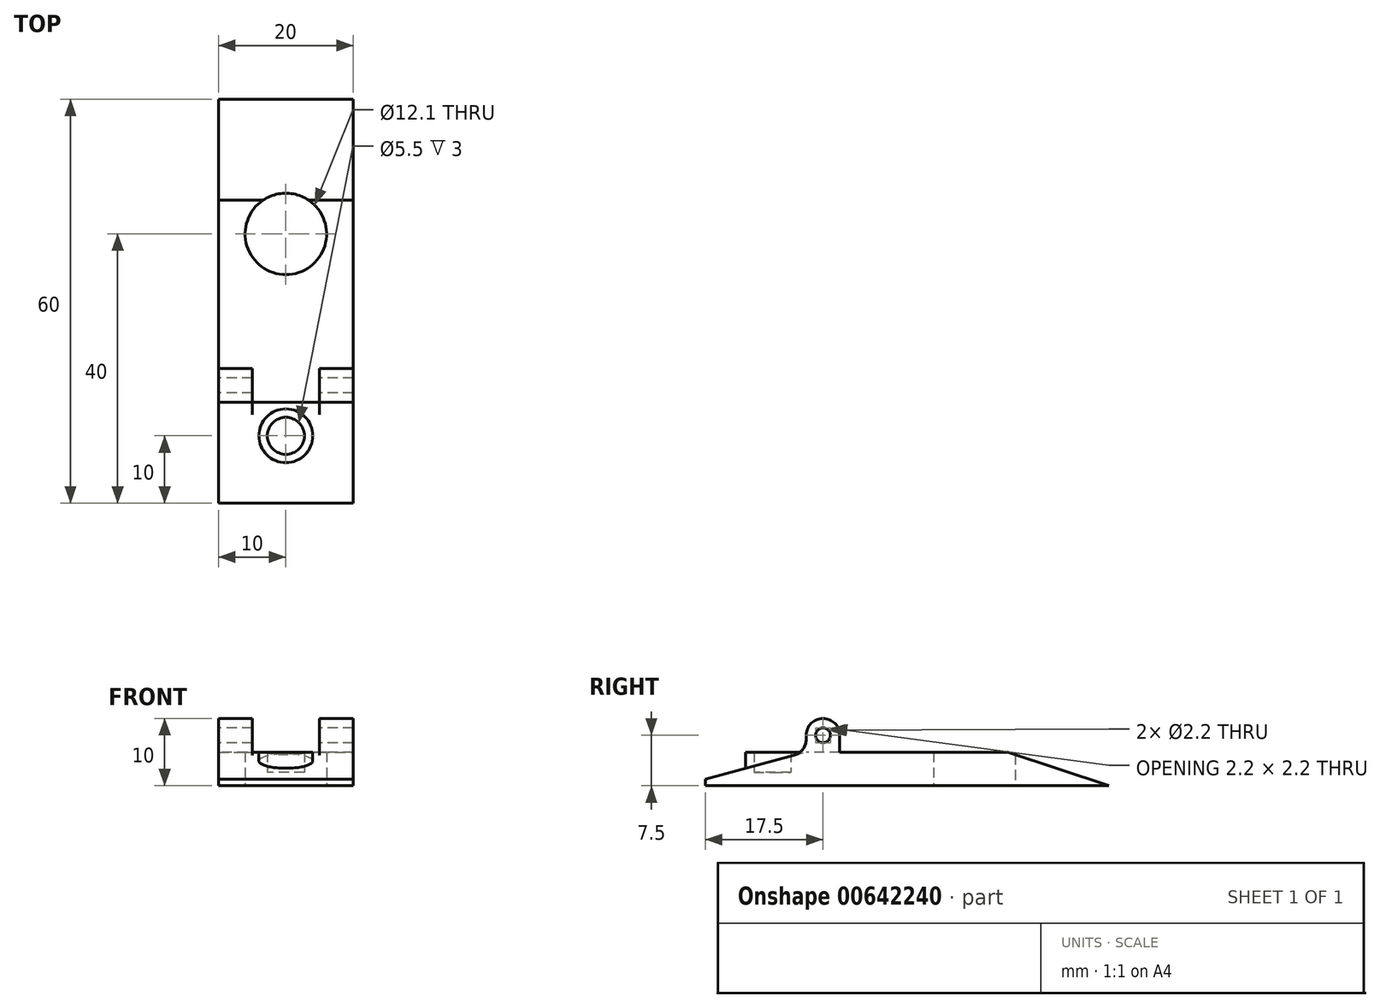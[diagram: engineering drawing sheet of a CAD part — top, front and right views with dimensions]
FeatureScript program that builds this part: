
annotation { "Feature Type Name" : "Feature", "Feature Type Description" : "" }
export const myFeature = defineFeature(function(context is Context, id is Id, definition is map)
    precondition{}
    {
        {
            var Q0;
            Q0=qCreatedBy(makeId("Top.planeOp"),FACE);
            var sketch = newSketch(context, id + "F0", { "sketchPlane" : qUnion([Q0])});
            skLineSegment(sketch, "E0.bottom", {"start": v(0, 0) * mm, "end": v(20, 0) * mm});
            skLineSegment(sketch, "E0.top", {"start": v(0, 60) * mm, "end": v(20, 60) * mm});
            skLineSegment(sketch, "E0.left", {"start": v(0, 0) * mm, "end": v(0, 60) * mm});
            skLineSegment(sketch, "E0.right", {"start": v(20, 0) * mm, "end": v(20, 60) * mm});
            skCircle(sketch, "E1", {"center": v(10, 40) * mm, "radius": 6.05 * mm});
            skCircle(sketch, "E2", {"center": v(10, 10) * mm, "radius": 2.75 * mm});
            skCircle(sketch, "E3", {"center": v(10, 40) * mm, "radius": 2 * mm});
            skCircle(sketch, "E4", {"center": v(10, 10) * mm, "radius": 4 * mm});
            skSolve(sketch);
        }
        {
            var Q0;
            Q0=makeQuery(id+"F0.imprint","IMPRINT",FACE,{"disambiguationData":[TD([[makeQuery(id+"F0.imprint","IMPRINT",EDGE,{"derivedFrom":sQuery(id+"F0.wireOp",EDGE,"E0.bottom")}),1.0]])]});
            extrude(context, id + "F1", {"entities" : qUnion([Q0]), "depth" : 4 * mm, "offsetDistance" : 25 * mm});
        }
        {
            var Q0;
            Q0=makeQuery(id+"F1.opExtrude","CAP_FACE",FACE,{"disambiguationData":[OSD([sQuery(id+"F0.wireOp",EDGE,"E0.bottom"),sQuery(id+"F0.wireOp",EDGE,"E0.top"),sQuery(id+"F0.wireOp",EDGE,"E0.left"),sQuery(id+"F0.wireOp",EDGE,"E0.right"),sQuery(id+"F0.wireOp",EDGE,"E1")])],"isStart":false});
            var Q1;
            Q1=makeQuery(id+"F0.imprint","IMPRINT",FACE,{"disambiguationData":[TD([[makeQuery(id+"F0.imprint","IMPRINT",EDGE,{"derivedFrom":sQuery(id+"F0.wireOp",EDGE,"E2")}),-1.0]])]});
            extrude(context, id + "F2", {"entities" : qUnion([Q0, Q1]), "operationType" : NewBodyOperationType.ADD, "depth" : 1 * mm, "offsetDistance" : 25 * mm});
        }
        {
            var Q0;
            Q0=makeQuery(id+"F2.opExtrude","CAP_FACE",FACE,{"disambiguationData":[OSD([sQuery(id+"F0.wireOp",EDGE,"E0.bottom"),sQuery(id+"F0.wireOp",EDGE,"E0.top"),sQuery(id+"F0.wireOp",EDGE,"E0.left"),sQuery(id+"F0.wireOp",EDGE,"E0.right"),sQuery(id+"F0.wireOp",EDGE,"E1")])],"isStart":false});
            var sketch = newSketch(context, id + "F3", { "sketchPlane" : qUnion([Q0])});
            skLineSegment(sketch, "E5.bottom", {"start": v(0, 15) * mm, "end": v(20, 15) * mm});
            skLineSegment(sketch, "E5.top", {"start": v(0, 20) * mm, "end": v(20, 20) * mm});
            skLineSegment(sketch, "E5.left", {"start": v(0, 15) * mm, "end": v(0, 20) * mm});
            skLineSegment(sketch, "E5.right", {"start": v(20, 15) * mm, "end": v(20, 20) * mm});
            skLineSegment(sketch, "E6.bottom", {"start": v(5, 20) * mm, "end": v(15, 20) * mm});
            skLineSegment(sketch, "E6.top", {"start": v(5, 15) * mm, "end": v(15, 15) * mm});
            skLineSegment(sketch, "E6.left", {"start": v(5, 20) * mm, "end": v(5, 15) * mm});
            skLineSegment(sketch, "E6.right", {"start": v(15, 20) * mm, "end": v(15, 15) * mm});
            skSolve(sketch);
        }
        {
            var Q0;
            {var subQ0=sQuery(id+"F3.wireOp",EDGE,"E5.left");Q0=makeQuery(id+"F3.imprint","IMPRINT",FACE,{"disambiguationData":[TD([[makeQuery(id+"F3.imprint","IMPRINT",EDGE,{"derivedFrom":subQ0}),-1.0]])]});}
            var Q1;
            {var subQ0=sQuery(id+"F3.wireOp",EDGE,"E5.right");Q1=makeQuery(id+"F3.imprint","IMPRINT",FACE,{"disambiguationData":[TD([[makeQuery(id+"F3.imprint","IMPRINT",EDGE,{"derivedFrom":subQ0}),1.0]])]});}
            extrude(context, id + "F4", {"entities" : qUnion([Q0, Q1]), "operationType" : NewBodyOperationType.ADD, "depth" : 5 * mm, "offsetDistance" : 25 * mm});
        }
        {
            var Q0;
            Q0=makeQuery(id+"F2.opExtrude","CAP_EDGE",EDGE,{"disambiguationData":[OSD([sQuery(id+"F0.wireOp",EDGE,"E0.bottom")])],"isStart":false});
            chamfer(context, id + "F5", {"entities" : qUnion([Q0]), "chamferType" : ChamferType.TWO_OFFSETS, "width1" : 15 * mm, "oppositeDirection" : false, "width2" : 4 * mm, "tangentPropagation" : true});
        }
        {
            var Q0;
            {var subQ0=sQuery(id+"F3.wireOp",EDGE,"E5.bottom");Q0=makeQuery(id+"F5.opChamfer","BLEND_EDGE",EDGE,{"blendedFrom":[makeQuery(id+"F2.opExtrude","CAP_EDGE",EDGE,{"disambiguationData":[OSD([sQuery(id+"F0.wireOp",EDGE,"E0.bottom")])],"isStart":false}),makeQuery(id+"F4.opExtrude","SWEPT_FACE",FACE,{"disambiguationData":[OSD([subQ0]),TDD([makeQuery(id+"F3.imprint","IMPRINT",EDGE,{"disambiguationData":[TD([[makeQuery(id+"F3.imprint","INTERSECT",VERTEX,{"derivedFrom":[makeQuery(id+"F2.opExtrude","CAP_EDGE",EDGE,{"disambiguationData":[OSD([sQuery(id+"F0.wireOp",EDGE,"E0.left")])],"isStart":false}),subQ0,sQuery(id+"F3.wireOp",EDGE,"E5.left")]}),-1.0]])],"derivedFrom":subQ0})])]})],"blendedInto":[makeQuery(id+"F4.opExtrude","SWEPT_FACE",FACE,{"disambiguationData":[OSD([subQ0]),TDD([makeQuery(id+"F3.imprint","IMPRINT",EDGE,{"disambiguationData":[TD([[makeQuery(id+"F3.imprint","INTERSECT",VERTEX,{"derivedFrom":[makeQuery(id+"F2.opExtrude","CAP_EDGE",EDGE,{"disambiguationData":[OSD([sQuery(id+"F0.wireOp",EDGE,"E0.left")])],"isStart":false}),subQ0,sQuery(id+"F3.wireOp",EDGE,"E5.left")]}),-1.0]])],"derivedFrom":subQ0})])]})]});}
            var Q1;
            {var subQ0=sQuery(id+"F3.wireOp",EDGE,"E5.bottom");Q1=makeQuery(id+"F4.opExtrude","CAP_EDGE",EDGE,{"disambiguationData":[OSD([subQ0]),TDD([makeQuery(id+"F3.imprint","IMPRINT",EDGE,{"disambiguationData":[TD([[makeQuery(id+"F3.imprint","INTERSECT",VERTEX,{"derivedFrom":[makeQuery(id+"F2.opExtrude","CAP_EDGE",EDGE,{"disambiguationData":[OSD([sQuery(id+"F0.wireOp",EDGE,"E0.left")])],"isStart":false}),subQ0,sQuery(id+"F3.wireOp",EDGE,"E5.left")]}),-1.0]])],"derivedFrom":subQ0})])],"isStart":false});}
            var Q2;
            {var subQ0=sQuery(id+"F3.wireOp",EDGE,"E5.bottom");Q2=makeQuery(id+"F5.opChamfer","BLEND_EDGE",EDGE,{"blendedFrom":[makeQuery(id+"F2.opExtrude","CAP_EDGE",EDGE,{"disambiguationData":[OSD([sQuery(id+"F0.wireOp",EDGE,"E0.bottom")])],"isStart":false}),makeQuery(id+"F4.opExtrude","SWEPT_FACE",FACE,{"disambiguationData":[OSD([subQ0]),TDD([makeQuery(id+"F3.imprint","IMPRINT",EDGE,{"disambiguationData":[TD([[makeQuery(id+"F3.imprint","INTERSECT",VERTEX,{"derivedFrom":[makeQuery(id+"F2.opExtrude","CAP_EDGE",EDGE,{"disambiguationData":[OSD([sQuery(id+"F0.wireOp",EDGE,"E0.right")])],"isStart":false}),subQ0,sQuery(id+"F3.wireOp",EDGE,"E5.right")]}),1.0]])],"derivedFrom":subQ0})])]})],"blendedInto":[makeQuery(id+"F4.opExtrude","SWEPT_FACE",FACE,{"disambiguationData":[OSD([subQ0]),TDD([makeQuery(id+"F3.imprint","IMPRINT",EDGE,{"disambiguationData":[TD([[makeQuery(id+"F3.imprint","INTERSECT",VERTEX,{"derivedFrom":[makeQuery(id+"F2.opExtrude","CAP_EDGE",EDGE,{"disambiguationData":[OSD([sQuery(id+"F0.wireOp",EDGE,"E0.right")])],"isStart":false}),subQ0,sQuery(id+"F3.wireOp",EDGE,"E5.right")]}),1.0]])],"derivedFrom":subQ0})])]})]});}
            var Q3;
            {var subQ0=sQuery(id+"F3.wireOp",EDGE,"E5.bottom");Q3=makeQuery(id+"F4.opExtrude","CAP_EDGE",EDGE,{"disambiguationData":[OSD([subQ0]),TDD([makeQuery(id+"F3.imprint","IMPRINT",EDGE,{"disambiguationData":[TD([[makeQuery(id+"F3.imprint","INTERSECT",VERTEX,{"derivedFrom":[makeQuery(id+"F2.opExtrude","CAP_EDGE",EDGE,{"disambiguationData":[OSD([sQuery(id+"F0.wireOp",EDGE,"E0.right")])],"isStart":false}),subQ0,sQuery(id+"F3.wireOp",EDGE,"E5.right")]}),1.0]])],"derivedFrom":subQ0})])],"isStart":false});}
            var Q4;
            {var subQ0=sQuery(id+"F3.wireOp",EDGE,"E5.top");Q4=makeQuery(id+"F4.opExtrude","CAP_EDGE",EDGE,{"disambiguationData":[OSD([subQ0]),TDD([makeQuery(id+"F3.imprint","IMPRINT",EDGE,{"disambiguationData":[TD([[makeQuery(id+"F3.imprint","INTERSECT",VERTEX,{"derivedFrom":[makeQuery(id+"F2.opExtrude","CAP_EDGE",EDGE,{"disambiguationData":[OSD([sQuery(id+"F0.wireOp",EDGE,"E0.left")])],"isStart":false}),subQ0,sQuery(id+"F3.wireOp",EDGE,"E5.left")]}),-1.0]])],"derivedFrom":subQ0})])],"isStart":false});}
            var Q5;
            {var subQ0=sQuery(id+"F3.wireOp",EDGE,"E5.top");Q5=makeQuery(id+"F4.opExtrude","CAP_EDGE",EDGE,{"disambiguationData":[OSD([subQ0]),TDD([makeQuery(id+"F3.imprint","IMPRINT",EDGE,{"disambiguationData":[TD([[makeQuery(id+"F3.imprint","INTERSECT",VERTEX,{"derivedFrom":[makeQuery(id+"F2.opExtrude","CAP_EDGE",EDGE,{"disambiguationData":[OSD([sQuery(id+"F0.wireOp",EDGE,"E0.right")])],"isStart":false}),subQ0,sQuery(id+"F3.wireOp",EDGE,"E5.right")]}),1.0]])],"derivedFrom":subQ0})])],"isStart":false});}
            fillet(context, id + "F6", {"entities" : qUnion([Q0, Q1, Q2, Q3, Q4, Q5]), "radius" : 2.5 * mm, "tangentPropagation" : true, "allowEdgeOverflow" : false});
        }
        {
            var Q0;
            {var subQ0=sQuery(id+"F0.wireOp",EDGE,"E0.left");Q0=makeQuery(id+"F4.boolean.opBoolean","MERGE",FACE,{"derivedFrom":[makeQuery(id+"F2.boolean.opBoolean","MERGE",FACE,{"derivedFrom":[makeQuery(id+"F1.opExtrude","SWEPT_FACE",FACE,{"disambiguationData":[OSD([subQ0])]}),makeQuery(id+"F2.opExtrude","SWEPT_FACE",FACE,{"disambiguationData":[OSD([subQ0])]})]}),makeQuery(id+"F4.opExtrude","SWEPT_FACE",FACE,{"disambiguationData":[OSD([sQuery(id+"F3.wireOp",EDGE,"E5.left")])]})]});}
            var sketch = newSketch(context, id + "F7", { "sketchPlane" : qUnion([Q0])});
            skCircle(sketch, "E7", {"center": v(-17.5, 7.5) * mm, "radius": 1.1 * mm});
            skSolve(sketch);
        }
        {
            var Q0;
            Q0=makeQuery(id+"F7.imprint","IMPRINT",FACE,{"disambiguationData":[TD([[makeQuery(id+"F7.imprint","IMPRINT",EDGE,{"derivedFrom":sQuery(id+"F7.wireOp",EDGE,"E7")}),1.0]])]});
            extrude(context, id + "F8", {"entities" : qUnion([Q0]), "operationType" : NewBodyOperationType.REMOVE, "oppositeDirection" : true, "depth" : 25 * mm, "offsetDistance" : 25 * mm});
        }
        {
            var Q0;
            Q0=makeQuery(id+"F0.imprint","IMPRINT",FACE,{"disambiguationData":[TD([[makeQuery(id+"F0.imprint","IMPRINT",EDGE,{"derivedFrom":sQuery(id+"F0.wireOp",EDGE,"E2")}),-1.0]])]});
            extrude(context, id + "F9", {"entities" : qUnion([Q0]), "depth" : 5 * mm, "offsetDistance" : 25 * mm});
        }
        {
            var Q0;
            Q0=makeQuery(id+"F2.opExtrude","CAP_EDGE",EDGE,{"disambiguationData":[OSD([sQuery(id+"F0.wireOp",EDGE,"E0.top")])],"isStart":false});
            chamfer(context, id + "F10", {"entities" : qUnion([Q0]), "chamferType" : ChamferType.TWO_OFFSETS, "width1" : 5 * mm, "oppositeDirection" : false, "width2" : 15 * mm, "tangentPropagation" : true});
        }
        {
            var Q0;
            Q0=makeQuery(id+"F0.imprint","IMPRINT",FACE,{"disambiguationData":[TD([[makeQuery(id+"F0.imprint","IMPRINT",EDGE,{"derivedFrom":sQuery(id+"F0.wireOp",EDGE,"E2")}),1.0]])]});
            extrude(context, id + "F11", {"entities" : qUnion([Q0]), "operationType" : NewBodyOperationType.ADD, "depth" : 2 * mm, "offsetDistance" : 25 * mm});
        }
    });
